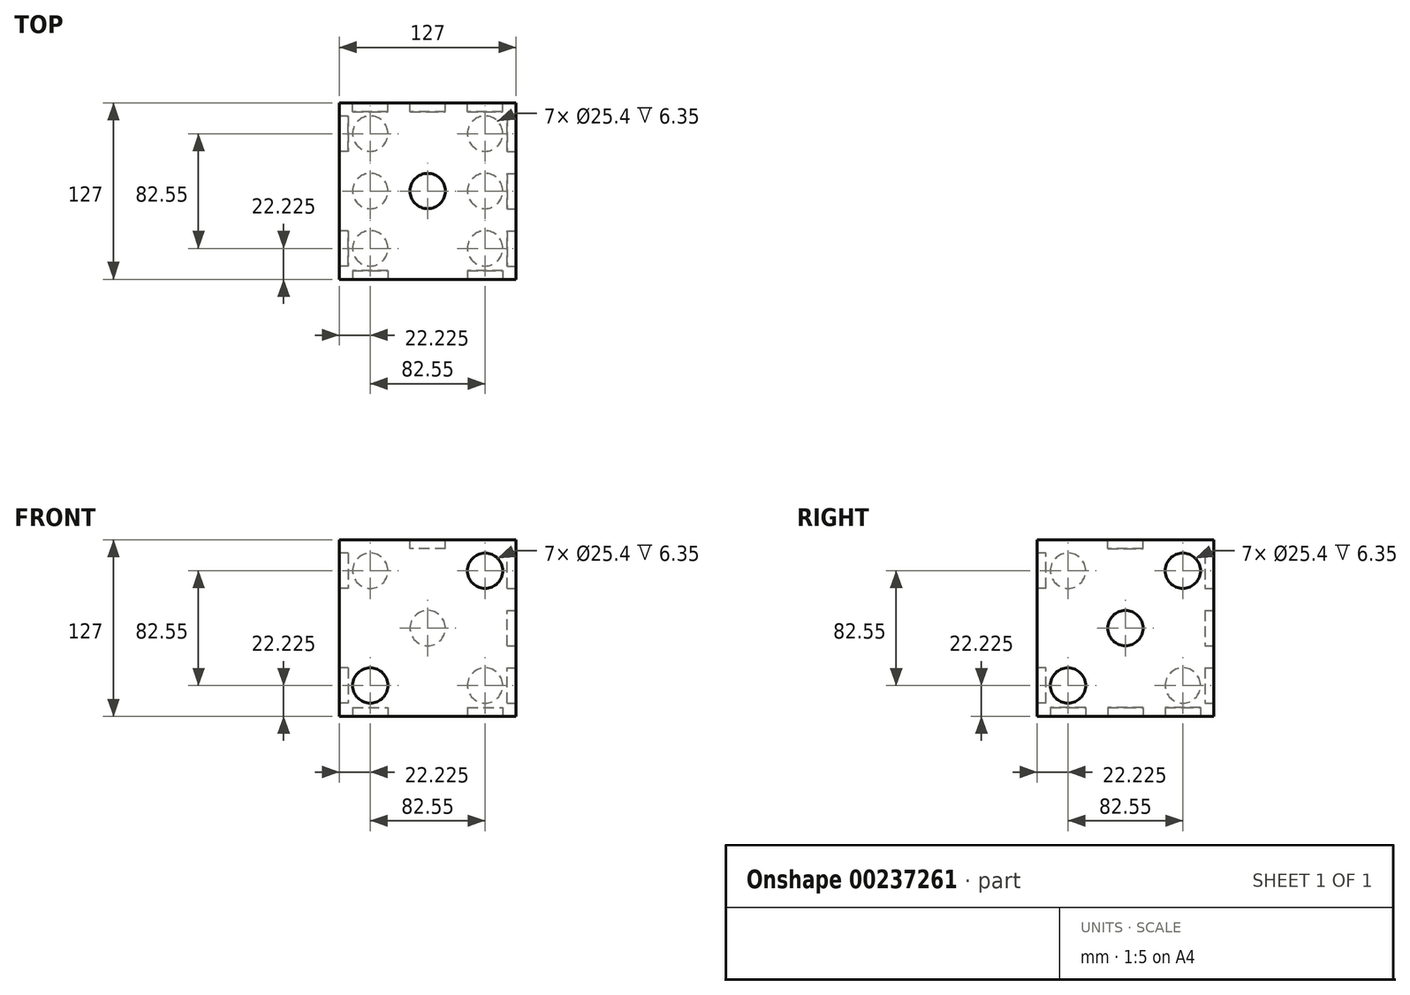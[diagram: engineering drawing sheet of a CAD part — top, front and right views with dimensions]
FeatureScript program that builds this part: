
annotation { "Feature Type Name" : "Feature", "Feature Type Description" : "" }
export const myFeature = defineFeature(function(context is Context, id is Id, definition is map)
    precondition{}
    {
        {
            var Q0;
            Q0=qCreatedBy(makeId("Top.planeOp"),FACE);
            var sketch = newSketch(context, id + "F0", { "sketchPlane" : qUnion([Q0])});
            skLineSegment(sketch, "E0.bottom", {"start": v(0, 0) * mm, "end": v(127, 0) * mm});
            skLineSegment(sketch, "E0.top", {"start": v(0, 127) * mm, "end": v(127, 127) * mm});
            skLineSegment(sketch, "E0.left", {"start": v(0, 0) * mm, "end": v(0, 127) * mm});
            skLineSegment(sketch, "E0.right", {"start": v(127, 0) * mm, "end": v(127, 127) * mm});
            skSolve(sketch);
        }
        {
            var Q0;
            Q0=makeQuery(id+"F0.imprint","IMPRINT",FACE,{"disambiguationData":[TD([[makeQuery(id+"F0.imprint","IMPRINT",EDGE,{"derivedFrom":sQuery(id+"F0.wireOp",EDGE,"E0.bottom")}),1.0]])]});
            extrude(context, id + "F1", {"entities" : qUnion([Q0]), "depth" : 127 * mm});
        }
        {
            var Q0;
            Q0=makeQuery(id+"F1.opExtrude","CAP_FACE",FACE,{"disambiguationData":[OSD([sQuery(id+"F0.wireOp",EDGE,"E0.bottom"),sQuery(id+"F0.wireOp",EDGE,"E0.top"),sQuery(id+"F0.wireOp",EDGE,"E0.left"),sQuery(id+"F0.wireOp",EDGE,"E0.right")])],"isStart":false});
            var sketch = newSketch(context, id + "F2", { "sketchPlane" : qUnion([Q0])});
            skCircle(sketch, "E1", {"center": v(63.5, 63.5) * mm, "radius": 12.7 * mm});
            skPoint(sketch, "E1.centerSnap0", {"position": v(63.5, 127) * mm});
            skSolve(sketch);
        }
        {
            var Q0;
            Q0=makeQuery(id+"F2.imprint","IMPRINT",FACE,{"disambiguationData":[TD([[makeQuery(id+"F2.imprint","IMPRINT",EDGE,{"derivedFrom":sQuery(id+"F2.wireOp",EDGE,"E1")}),1.0]])]});
            var Q1;
            Q1=sQuery(id+"F2.wireOp",EDGE,"E1");
            extrude(context, id + "F3", {"entities" : qUnion([Q0]), "operationType" : NewBodyOperationType.REMOVE, "surfaceEntities" : qUnion([Q1]), "oppositeDirection" : true, "depth" : 6.35 * mm});
        }
        {
            var Q0;
            Q0=makeQuery(id+"F1.opExtrude","SWEPT_FACE",FACE,{"disambiguationData":[OSD([sQuery(id+"F0.wireOp",EDGE,"E0.bottom")])]});
            var sketch = newSketch(context, id + "F4", { "sketchPlane" : qUnion([Q0])});
            skCircle(sketch, "E2", {"center": v(22.23, 22.23) * mm, "radius": 12.7 * mm});
            skCircle(sketch, "E3", {"center": v(104.77, 104.78) * mm, "radius": 12.7 * mm});
            skSolve(sketch);
        }
        {
            var Q0;
            Q0 = qSketchRegion(id + "F4", true);
            extrude(context, id + "F5", {"entities" : qUnion([Q0]), "operationType" : NewBodyOperationType.REMOVE, "oppositeDirection" : true, "depth" : 6.35 * mm});
        }
        {
            var Q0;
            Q0=makeQuery(id+"F1.opExtrude","SWEPT_FACE",FACE,{"disambiguationData":[OSD([sQuery(id+"F0.wireOp",EDGE,"E0.right")])]});
            var sketch = newSketch(context, id + "F6", { "sketchPlane" : qUnion([Q0])});
            skLineSegment(sketch, "E4", {"start": v(0, 0) * mm, "end": v(127, 127) * mm, "construction": true});
            skCircle(sketch, "E5", {"center": v(22.22, 22.23) * mm, "radius": 12.7 * mm});
            skCircle(sketch, "E6", {"center": v(63.5, 63.5) * mm, "radius": 12.7 * mm});
            skCircle(sketch, "E7", {"center": v(104.77, 104.78) * mm, "radius": 12.7 * mm});
            skSolve(sketch);
        }
        {
            var Q0;
            Q0 = qSketchRegion(id + "F6", true);
            extrude(context, id + "F7", {"entities" : qUnion([Q0]), "operationType" : NewBodyOperationType.REMOVE, "oppositeDirection" : true, "depth" : 6.35 * mm});
        }
        {
            var Q0;
            Q0=makeQuery(id+"F1.opExtrude","SWEPT_FACE",FACE,{"disambiguationData":[OSD([sQuery(id+"F0.wireOp",EDGE,"E0.left")])]});
            var sketch = newSketch(context, id + "F8", { "sketchPlane" : qUnion([Q0])});
            skCircle(sketch, "E8", {"center": v(-104.78, 22.23) * mm, "radius": 12.7 * mm});
            skCircle(sketch, "E9", {"center": v(-22.22, 22.23) * mm, "radius": 12.7 * mm});
            skCircle(sketch, "E10", {"center": v(-22.23, 104.78) * mm, "radius": 12.7 * mm});
            skCircle(sketch, "E11", {"center": v(-104.78, 104.78) * mm, "radius": 12.7 * mm});
            skSolve(sketch);
        }
        {
            var Q0;
            Q0 = qSketchRegion(id + "F8", true);
            extrude(context, id + "F9", {"entities" : qUnion([Q0]), "operationType" : NewBodyOperationType.REMOVE, "oppositeDirection" : true, "depth" : 6.35 * mm});
        }
        {
            var Q0;
            Q0=makeQuery(id+"F1.opExtrude","SWEPT_FACE",FACE,{"disambiguationData":[OSD([sQuery(id+"F0.wireOp",EDGE,"E0.top")])]});
            var sketch = newSketch(context, id + "F10", { "sketchPlane" : qUnion([Q0])});
            skCircle(sketch, "E12", {"center": v(-104.77, 22.23) * mm, "radius": 12.7 * mm});
            skCircle(sketch, "E13", {"center": v(-22.22, 22.23) * mm, "radius": 12.7 * mm});
            skCircle(sketch, "E14", {"center": v(-22.23, 104.78) * mm, "radius": 12.7 * mm});
            skCircle(sketch, "E15", {"center": v(-104.77, 104.78) * mm, "radius": 12.7 * mm});
            skCircle(sketch, "E16", {"center": v(-63.5, 63.5) * mm, "radius": 12.7 * mm});
            skSolve(sketch);
        }
        {
            var Q0;
            Q0 = qSketchRegion(id + "F10", true);
            extrude(context, id + "F11", {"entities" : qUnion([Q0]), "operationType" : NewBodyOperationType.REMOVE, "oppositeDirection" : true, "depth" : 6.35 * mm});
        }
        {
            var Q0;
            Q0=makeQuery(id+"F1.opExtrude","CAP_FACE",FACE,{"disambiguationData":[OSD([sQuery(id+"F0.wireOp",EDGE,"E0.bottom"),sQuery(id+"F0.wireOp",EDGE,"E0.top"),sQuery(id+"F0.wireOp",EDGE,"E0.left"),sQuery(id+"F0.wireOp",EDGE,"E0.right")])],"isStart":true});
            var sketch = newSketch(context, id + "F12", { "sketchPlane" : qUnion([Q0])});
            skCircle(sketch, "E17", {"center": v(22.23, -63.5) * mm, "radius": 12.7 * mm});
            skCircle(sketch, "E18", {"center": v(104.78, -104.78) * mm, "radius": 12.7 * mm});
            skCircle(sketch, "E19", {"center": v(104.78, -63.5) * mm, "radius": 12.7 * mm});
            skPoint(sketch, "E19.centerSnap0", {"position": v(127, -63.5) * mm});
            skCircle(sketch, "E20", {"center": v(104.77, -22.23) * mm, "radius": 12.7 * mm});
            skCircle(sketch, "E21", {"center": v(22.23, -104.78) * mm, "radius": 12.7 * mm});
            skCircle(sketch, "E22", {"center": v(22.22, -22.22) * mm, "radius": 12.7 * mm});
            skSolve(sketch);
        }
        {
            var Q0;
            Q0 = qSketchRegion(id + "F12", true);
            extrude(context, id + "F13", {"entities" : qUnion([Q0]), "operationType" : NewBodyOperationType.REMOVE, "oppositeDirection" : true, "depth" : 6.35 * mm});
        }
    });
